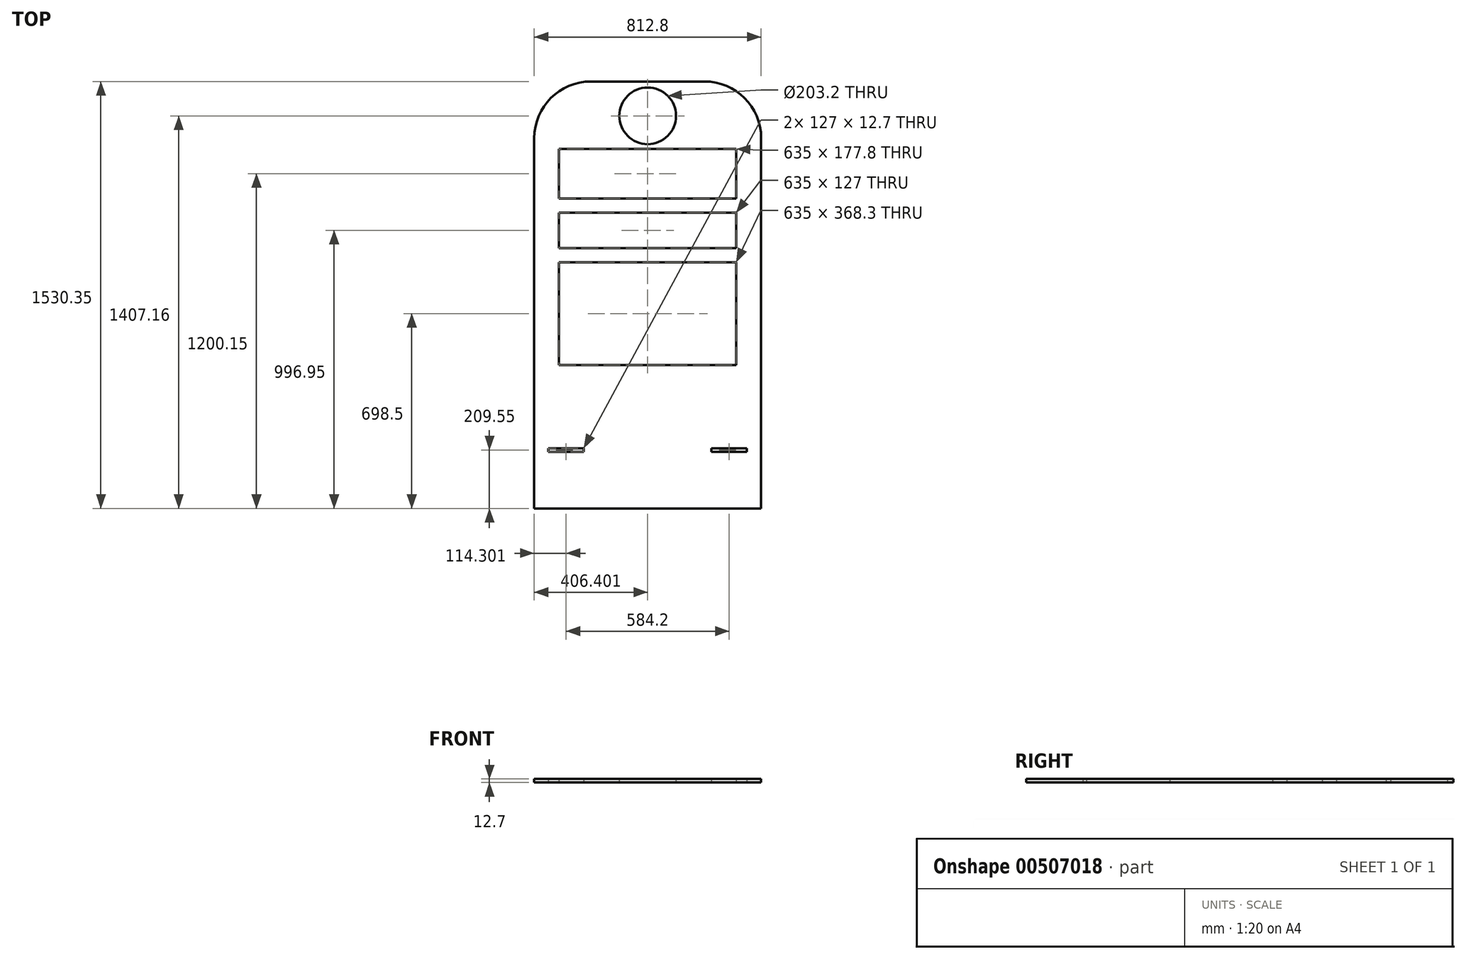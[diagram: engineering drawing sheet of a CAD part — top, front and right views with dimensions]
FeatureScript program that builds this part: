
annotation { "Feature Type Name" : "Feature", "Feature Type Description" : "" }
export const myFeature = defineFeature(function(context is Context, id is Id, definition is map)
    precondition{}
    {
        {
            var Q0;
            Q0=qCreatedBy(makeId("Top.planeOp"),FACE);
            var sketch = newSketch(context, id + "F0", { "sketchPlane" : qUnion([Q0])});
            skLineSegment(sketch, "E0.left", {"start": v(-648.04, 763.82) * mm, "end": v(-648.04, -556.98) * mm});
            skLineSegment(sketch, "E0.right", {"start": v(164.76, 763.82) * mm, "end": v(164.76, -556.98) * mm});
            skLineSegment(sketch, "E1.0", {"start": v(-559.14, -48.98) * mm, "end": v(75.86, -48.98) * mm});
            skLineSegment(sketch, "E2.0", {"start": v(-559.14, 725.72) * mm, "end": v(-559.14, 547.92) * mm});
            skLineSegment(sketch, "E3.0", {"start": v(-559.14, 725.72) * mm, "end": v(75.86, 725.72) * mm});
            skLineSegment(sketch, "E4.0", {"start": v(75.86, 725.72) * mm, "end": v(75.86, 547.92) * mm});
            skLineSegment(sketch, "E5.0", {"start": v(-559.14, 319.32) * mm, "end": v(75.86, 319.32) * mm});
            skLineSegment(sketch, "E6.trimOffspring", {"start": v(-559.14, 90.72) * mm, "end": v(-559.14, -48.98) * mm});
            skLineSegment(sketch, "E7.trimOffspring", {"start": v(75.86, 90.72) * mm, "end": v(75.86, -48.98) * mm});
            skLineSegment(sketch, "E8.trimOffspring", {"start": v(75.86, 319.32) * mm, "end": v(75.86, 141.52) * mm});
            skLineSegment(sketch, "E9.trimOffspring", {"start": v(-559.14, 319.32) * mm, "end": v(-559.14, 141.52) * mm});
            skLineSegment(sketch, "E10.trimOffspring", {"start": v(-559.14, 497.12) * mm, "end": v(-559.14, 370.12) * mm});
            skLineSegment(sketch, "E11.trimOffspring", {"start": v(75.86, 497.12) * mm, "end": v(75.86, 370.12) * mm});
            skLineSegment(sketch, "E12", {"start": v(-559.14, 370.12) * mm, "end": v(75.86, 370.12) * mm});
            skLineSegment(sketch, "E13", {"start": v(-559.14, 90.72) * mm, "end": v(-559.14, 141.52) * mm});
            skLineSegment(sketch, "E14", {"start": v(75.86, 90.72) * mm, "end": v(75.86, 141.52) * mm});
            skLineSegment(sketch, "E15", {"start": v(-559.14, 547.92) * mm, "end": v(75.86, 547.92) * mm});
            skLineSegment(sketch, "E16", {"start": v(75.86, 497.12) * mm, "end": v(-559.14, 497.12) * mm});
            skLineSegment(sketch, "E17", {"start": v(-444.84, 967.02) * mm, "end": v(-38.44, 967.02) * mm});
            skPoint(sketch, "E18.visualSharp", {"position": v(-648.04, 967.02) * mm});
            skArc(sketch, "E18.filletArc", {"start": v(-444.84, 967.02) * mm, "mid": v(-588.52, 907.5) * mm, "end": v(-648.04, 763.82) * mm});
            skPoint(sketch, "E19.visualSharp", {"position": v(164.76, 967.02) * mm});
            skArc(sketch, "E19.filletArc", {"start": v(164.76, 763.82) * mm, "mid": v(105.25, 907.5) * mm, "end": v(-38.44, 967.02) * mm});
            skLineSegment(sketch, "E20.0", {"start": v(-648.04, -563.33) * mm, "end": v(164.76, -563.33) * mm});
            skLineSegment(sketch, "E21", {"start": v(-648.04, -556.98) * mm, "end": v(-648.04, -563.33) * mm});
            skLineSegment(sketch, "E22", {"start": v(164.76, -556.98) * mm, "end": v(164.76, -563.33) * mm});
            skLineSegment(sketch, "E23.MirrorCS", {"start": v(-597.24, -360.13) * mm, "end": v(-597.24, -347.43) * mm});
            skLineSegment(sketch, "E24.MirrorCS", {"start": v(-470.24, -360.13) * mm, "end": v(-470.24, -347.43) * mm});
            skLineSegment(sketch, "E25.MirrorCS", {"start": v(113.96, -360.13) * mm, "end": v(113.96, -347.43) * mm});
            skLineSegment(sketch, "E26.MirrorCS", {"start": v(-13.04, -360.13) * mm, "end": v(-13.04, -347.43) * mm});
            skLineSegment(sketch, "E27.MirrorCS", {"start": v(-597.24, -360.13) * mm, "end": v(-470.24, -360.13) * mm});
            skLineSegment(sketch, "E28.MirrorCS", {"start": v(-13.04, -360.13) * mm, "end": v(113.96, -360.13) * mm});
            skLineSegment(sketch, "E29.MirrorCS", {"start": v(-597.24, -347.43) * mm, "end": v(-470.24, -347.43) * mm});
            skLineSegment(sketch, "E30.MirrorCS", {"start": v(-13.04, -347.43) * mm, "end": v(113.96, -347.43) * mm});
            skCircle(sketch, "E31", {"center": v(-241.64, 843.83) * mm, "radius": 101.6 * mm});
            skPoint(sketch, "E31.centerSnap0", {"position": v(-241.64, 725.72) * mm});
            skSolve(sketch);
        }
        {
            var Q0;
            Q0=makeQuery(id+"F0.imprint","IMPRINT",FACE,{"disambiguationData":[TD([[makeQuery(id+"F0.imprint","IMPRINT",EDGE,{"derivedFrom":sQuery(id+"F0.wireOp",EDGE,"E0.top")}),1.0]])]});
            var Q1;
            Q1=makeQuery(id+"F0.imprint","IMPRINT",FACE,{"disambiguationData":[TD([[makeQuery(id+"F0.imprint","IMPRINT",EDGE,{"derivedFrom":sQuery(id+"F0.wireOp",EDGE,"E0.left")}),1.0]])]});
            extrude(context, id + "F1", {"entities" : qUnion([Q0, Q1]), "depth" : 12.7 * mm, "offsetDistance" : 25.4 * mm});
        }
    });
